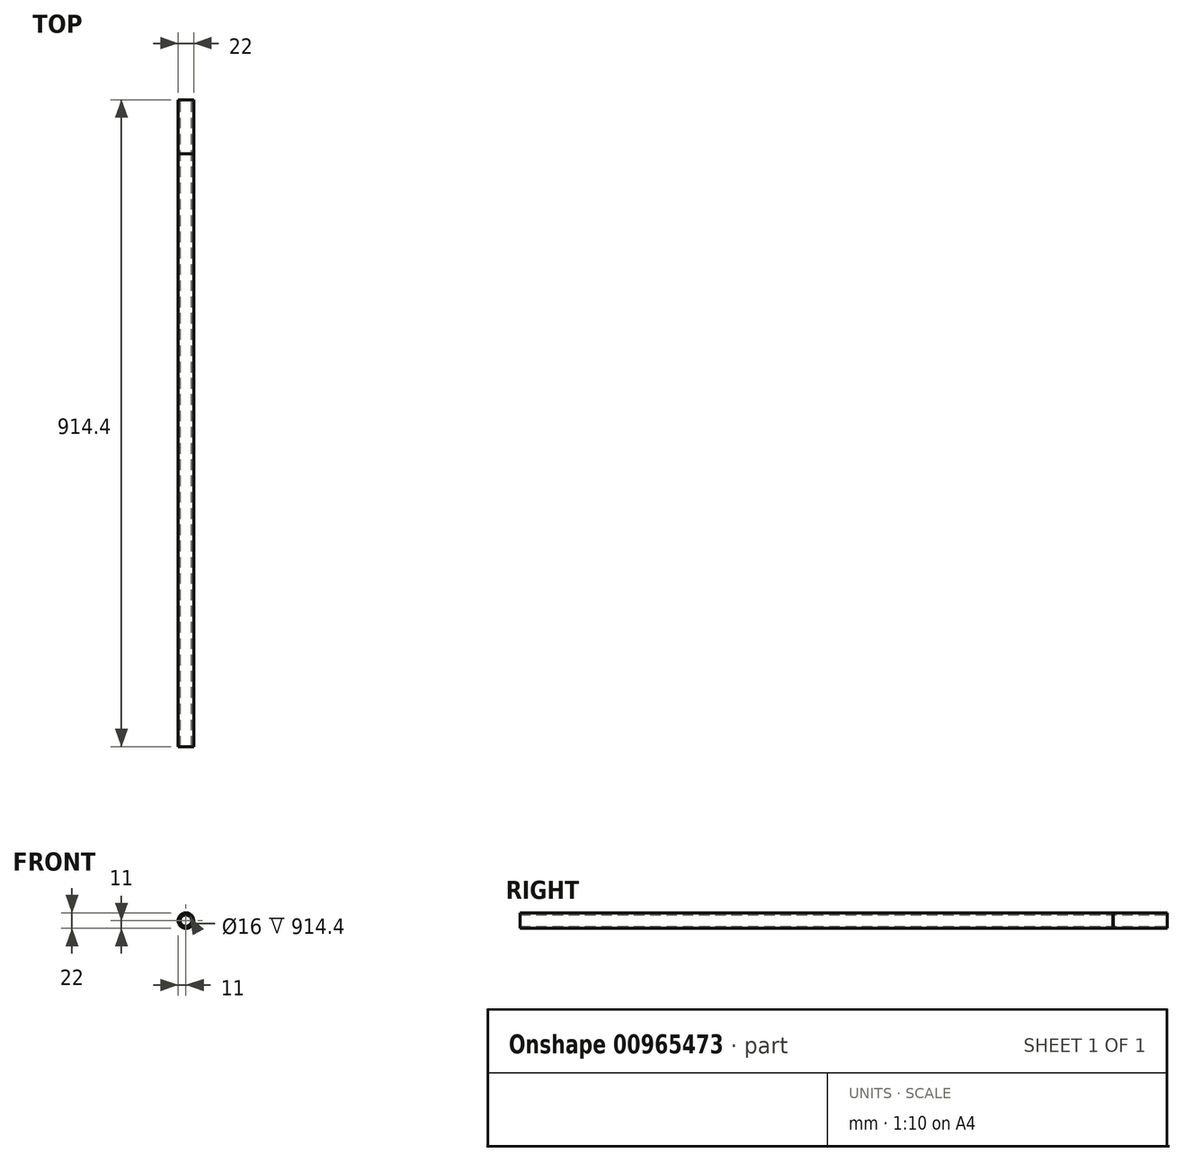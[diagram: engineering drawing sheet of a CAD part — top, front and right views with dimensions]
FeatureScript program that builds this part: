
annotation { "Feature Type Name" : "Feature", "Feature Type Description" : "" }
export const myFeature = defineFeature(function(context is Context, id is Id, definition is map)
    precondition{}
    {
        {
            var Q0;
            Q0=qCreatedBy(makeId("Front.planeOp"),FACE);
            var sketch = newSketch(context, id + "F0", { "sketchPlane" : qUnion([Q0])});
            skCircle(sketch, "E0", {"center": v(0, 0) * mm, "radius": 11 * mm});
            skCircle(sketch, "E1", {"center": v(0, 0) * mm, "radius": 8 * mm});
            skSolve(sketch);
        }
        {
            var Q0;
            Q0=makeQuery(id+"F0.imprint","IMPRINT",FACE,{"disambiguationData":[TD([[makeQuery(id+"F0.imprint","IMPRINT",EDGE,{"derivedFrom":sQuery(id+"F0.wireOp",EDGE,"E0")}),1.0]])]});
            extrude(context, id + "F1", {"entities" : qUnion([Q0]), "depth" : 914.4 * mm, "offsetDistance" : 25.4 * mm});
        }
        {
            var Q0;
            Q0=qCreatedBy(makeId("Front.planeOp"),FACE);
            cPlane(context, id + "F2", {"entities" : qUnion([Q0]), "cplaneType" : CPlaneType.OFFSET, "offset" : 76.2 * mm, "width" : 152.4 * mm, "height" : 152.4 * mm});
        }
        {
            var Q0;
            Q0=qCreatedBy(id+"F2.planeOp",FACE);
            var sketch = newSketch(context, id + "F3", { "sketchPlane" : qUnion([Q0])});
            skCircle(sketch, "E2", {"center": v(0, 0) * mm, "radius": 11 * mm});
            skCircle(sketch, "E3", {"center": v(0, 0) * mm, "radius": 10.66 * mm});
            skSolve(sketch);
        }
        {
            var Q0;
            Q0 = qSketchRegion(id + "F3", true);
            extrude(context, id + "F4", {"entities" : qUnion([Q0]), "operationType" : NewBodyOperationType.REMOVE, "depth" : 0.25 * mm, "offsetDistance" : 25.4 * mm});
        }
    });
